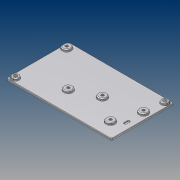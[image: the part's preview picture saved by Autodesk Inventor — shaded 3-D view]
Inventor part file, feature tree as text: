
AUTODESK INVENTOR PART (.ipt)
format: ipt  version: unknown  size: 720,384 bytes
history: native  units: mm (DEFAULTED — no unit token found)
features: sketch x7, extrude x6, fillet x4, plane x3, hole x1, other x1, shell x1, projected_geometry x1
ambient origin geometry x5: Origin, X Axis, Y Axis, Z Axis, Center Point
feature tree (24):
  extrude  "Base Profile"  Depth=125.1204mm
  extrude  "Extra Material for Screw Holes"  Depth=2.032mm
  hole  "Screw Holes"  [1 undecoded]
  extrude  "Extrusion3"  Depth=0.523599mm
  other  "Screw Hole Drafts"
  shell  "Screw Hole Shell"  Thickness=4.699mm
  extrude  "Velcro Cut"  Depth=31.75mm
  extrude  "Side Edge Clearance Cut"  Depth=57.15mm
  extrude  "Extrusion6"  Depth=54.61mm
  fillet  "Bottom Fillet 1"  Radius=8.89mm
  fillet  "Bottom Fillet 2"  Radius=20.32mm
  fillet  "Top Fillet 1"  Radius=44.45mm
  fillet  "Top Fillet 2"  [1 undecoded]
  plane  "YZ Plane (RIGHT)"
  plane  "XZ Plane (TOP)"
  plane  "XY Plane (FRONT)"
  sketch  "Sketch2"  dims[d0=74.3204mm d1=125.1204mm]
  sketch  "Sketch3"  dims[d2=1.778mm d3=2.032mm d4=-0.523599mm]
  sketch  "Sketch4"  dims[d5=2.4892mm d6=0.0mm]
  sketch  "Sketch5"  dims[d7=3.9624mm d8=12.7mm d9=6.477mm d10=2.4892mm d11=14.3117mm d12=19.05mm d13=20.594885mm d14=2.032mm]
  sketch  "Sketch6"  dims[d15=25.4mm d16=-0.349066mm d17=0.523599mm d18=4.699mm]
  sketch  "Sketch7"  dims[d19=57.15mm d20=31.75mm]
  projected_geometry  "Projected Loop1"
  sketch  "Sketch8"  dims[d21=31.75mm d22=57.15mm d23=54.61mm d24=8.89mm d25=20.32mm d26=44.45mm d27=0.0mm d28=14.605mm d29=12.7mm d30=13.335mm d31=29.21mm d32=57.15mm d33=20.0mm d35=360.0deg d39=34.925mm d40=6.35mm d41=0.762mm d42=-7.853982mm d43=0.762mm d44=27.94mm d45=44.45mm d46=1.27mm d47=0.762mm d48=0.523599mm d49=0.762mm d50=-1.745329mm d51=53.4416mm d52=2.54mm d53=6.0198mm d54=7.9502mm d55=3.175mm d56=0.79375mm d57=0.79375mm d58=0.254mm d59=0.79375mm d60=1.5875mm d61=0.396875mm d62=1.5875mm d63=0.79375mm d64=0.396875mm d65=0.396875mm d66=0.79375mm]
note: 2 required parameter values undecoded (feature->parameter linkage not recoverable at this tier; creation-order binding heuristic only, values carry confidence <= 0.55)
